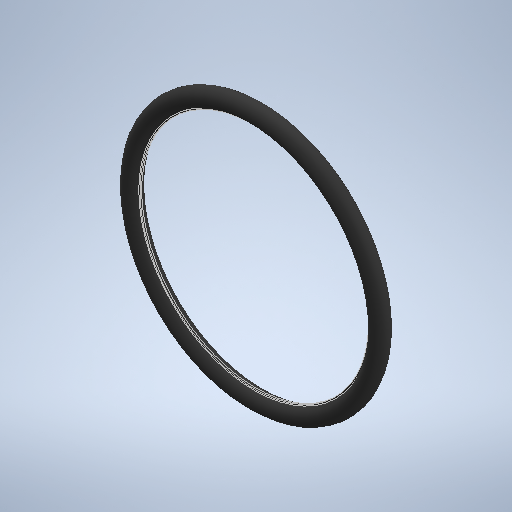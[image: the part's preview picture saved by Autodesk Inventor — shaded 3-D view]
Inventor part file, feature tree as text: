
AUTODESK INVENTOR PART (.ipt)
format: ipt  version: 2025 (Build 290162000, 162)  size: 306,688 bytes
history: native  units: in
note: dims shown in document units (in); Inventor stores cm internally (conversion verified against a paired STEP export)
features: extrude x1, sketch x1, revolve x1
ambient origin geometry x8: Origin, YZ Plane, XZ Plane, XY Plane, X Axis, Y Axis, Z Axis, Center Point
bodies: Solid1 (feature_tree)
feature tree (3):
  extrude  "Extrusion1"  [1 undecoded]
  sketch  "Sketch1"  dims[d0=0.0039in d1=0.0in]
  revolve  "Revolve1"  [1 undecoded]
note: 2 required parameter values undecoded (feature->parameter linkage not recoverable at this tier; creation-order binding heuristic only, values carry confidence <= 0.55)
